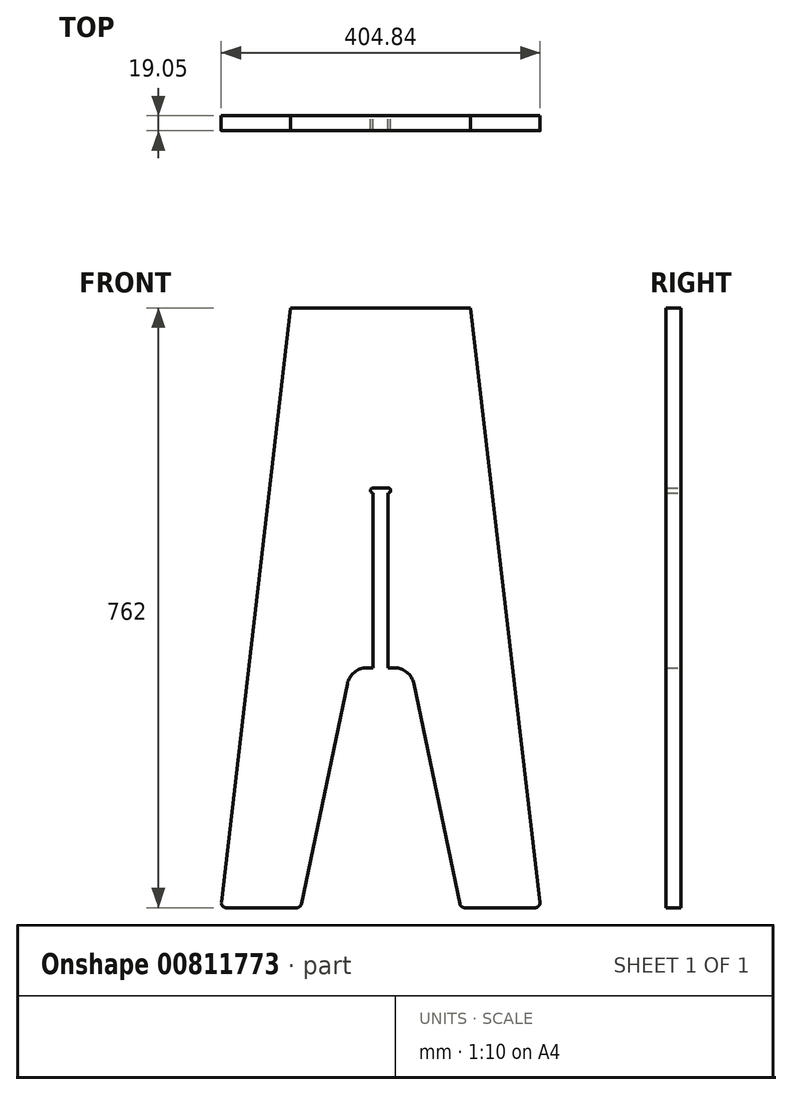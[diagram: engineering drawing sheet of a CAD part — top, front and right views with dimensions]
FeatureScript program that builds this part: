
annotation { "Feature Type Name" : "Feature", "Feature Type Description" : "" }
export const myFeature = defineFeature(function(context is Context, id is Id, definition is map)
    precondition{}
    {
        {
            var Q0;
            Q0=qCreatedBy(makeId("Front.planeOp"),FACE);
            var sketch = newSketch(context, id + "F0", { "sketchPlane" : qUnion([Q0])});
            skLineSegment(sketch, "E0", {"start": v(-202.37, -297.71) * mm, "end": v(-114.3, 457.2) * mm});
            skLineSegment(sketch, "E1", {"start": v(-114.3, 457.2) * mm, "end": v(9.52, 457.2) * mm});
            skLineSegment(sketch, "E2", {"start": v(-9.53, 228.6) * mm, "end": v(9.53, 228.6) * mm});
            skLineSegment(sketch, "E3", {"start": v(9.52, 457.2) * mm, "end": v(114.3, 457.2) * mm});
            skLineSegment(sketch, "E4", {"start": v(114.3, 457.2) * mm, "end": v(202.37, -297.71) * mm});
            skLineSegment(sketch, "E5", {"start": v(196.07, -304.8) * mm, "end": v(106.76, -304.8) * mm});
            skLineSegment(sketch, "E6", {"start": v(100.55, -299.75) * mm, "end": v(42.31, -20.22) * mm});
            skLineSegment(sketch, "E7", {"start": v(17.45, 0) * mm, "end": v(9.52, 0) * mm});
            skLineSegment(sketch, "E8", {"start": v(-42.31, -20.22) * mm, "end": v(-100.55, -299.75) * mm});
            skLineSegment(sketch, "E9", {"start": v(-106.76, -304.8) * mm, "end": v(-196.07, -304.8) * mm});
            skLineSegment(sketch, "E10", {"start": v(0, 228.6) * mm, "end": v(0, 0) * mm, "construction": true});
            skPoint(sketch, "E11.visualSharp", {"position": v(-203.2, -304.8) * mm});
            skArc(sketch, "E11.filletArc", {"start": v(-202.37, -297.71) * mm, "mid": v(-200.8, -302.67) * mm, "end": v(-196.07, -304.8) * mm});
            skPoint(sketch, "E12.visualSharp", {"position": v(-101.6, -304.8) * mm});
            skArc(sketch, "E12.filletArc", {"start": v(-106.76, -304.8) * mm, "mid": v(-102.76, -303.38) * mm, "end": v(-100.55, -299.75) * mm});
            skPoint(sketch, "E13.visualSharp", {"position": v(101.6, -304.8) * mm});
            skArc(sketch, "E13.filletArc", {"start": v(100.55, -299.75) * mm, "mid": v(102.76, -303.38) * mm, "end": v(106.76, -304.8) * mm});
            skPoint(sketch, "E14.visualSharp", {"position": v(203.2, -304.8) * mm});
            skArc(sketch, "E14.filletArc", {"start": v(196.07, -304.8) * mm, "mid": v(200.8, -302.67) * mm, "end": v(202.37, -297.71) * mm});
            skPoint(sketch, "E15.visualSharp", {"position": v(-38.1, 0) * mm});
            skArc(sketch, "E15.filletArc", {"start": v(-17.45, 0) * mm, "mid": v(-33.47, -5.7) * mm, "end": v(-42.31, -20.22) * mm});
            skPoint(sketch, "E16.visualSharp", {"position": v(38.1, 0) * mm});
            skArc(sketch, "E16.filletArc", {"start": v(42.31, -20.22) * mm, "mid": v(33.47, -5.7) * mm, "end": v(17.45, 0) * mm});
            skLineSegment(sketch, "E17.MirrorCS", {"start": v(-9.53, 0) * mm, "end": v(-9.53, 222) * mm});
            skLineSegment(sketch, "E18.MirrorCS", {"start": v(9.53, 222) * mm, "end": v(9.52, 0) * mm});
            skArc(sketch, "E19.MirrorCS", {"start": v(9.53, 228.6) * mm, "mid": v(12.83, 225.3) * mm, "end": v(9.53, 222) * mm});
            skArc(sketch, "E20.MirrorCS", {"start": v(-9.53, 222) * mm, "mid": v(-12.83, 225.3) * mm, "end": v(-9.53, 228.6) * mm});
            skPoint(sketch, "E21.orphan", {"position": v(-9.53, 457.2) * mm});
            skLineSegment(sketch, "E22.trimOffspring", {"start": v(-9.53, 0) * mm, "end": v(-17.45, 0) * mm});
            skSolve(sketch);
        }
        {
            var Q0;
            Q0=makeQuery(id+"F0.imprint","IMPRINT",FACE,{"disambiguationData":[TD([[makeQuery(id+"F0.imprint","IMPRINT",EDGE,{"derivedFrom":sQuery(id+"F0.wireOp",EDGE,"E0")}),-1.0]])]});
            extrude(context, id + "F1", {"entities" : qUnion([Q0]), "depth" : 19.05 * mm, "offsetDistance" : 25.4 * mm});
        }
    });
